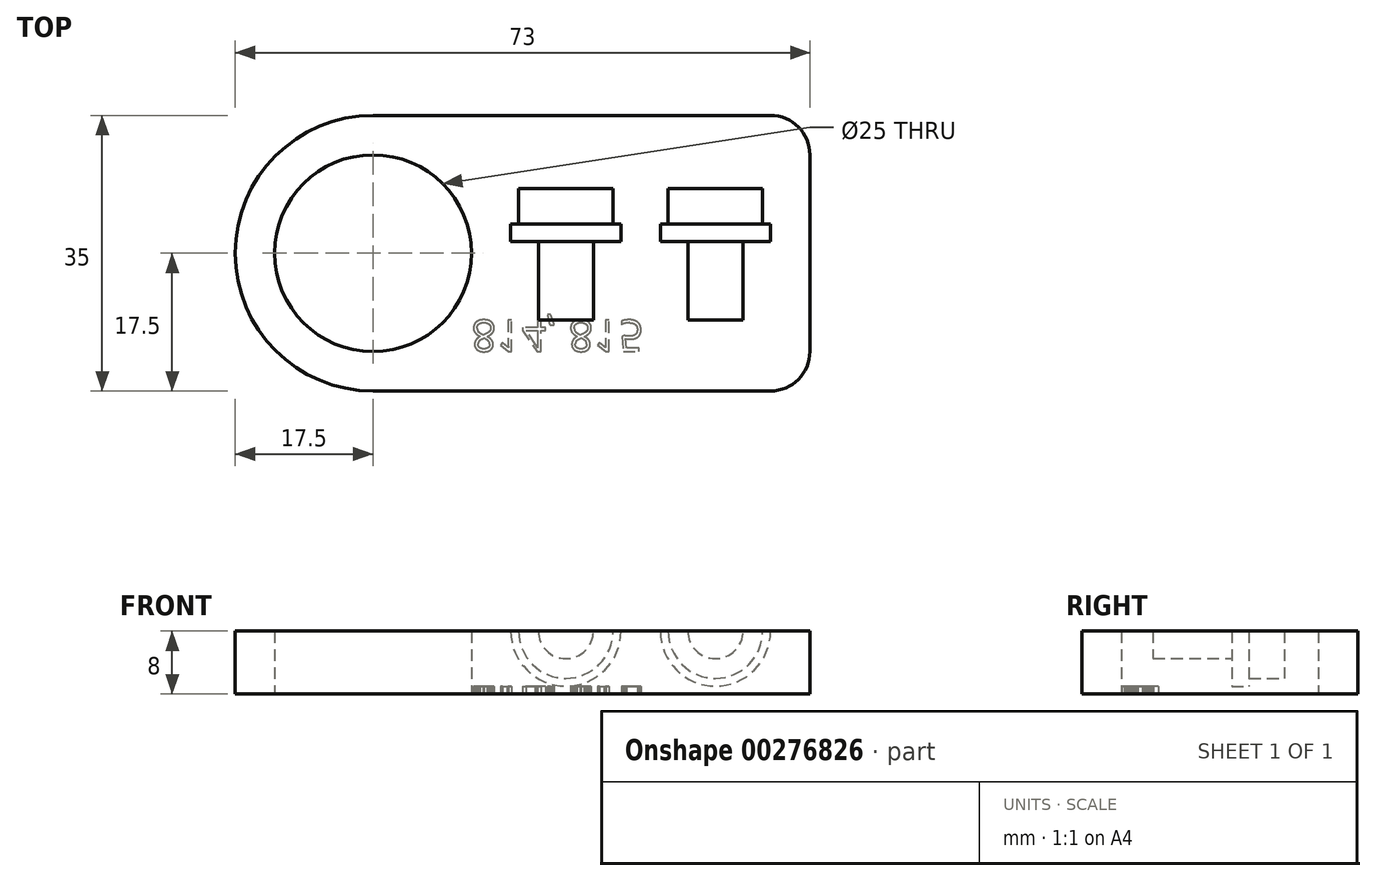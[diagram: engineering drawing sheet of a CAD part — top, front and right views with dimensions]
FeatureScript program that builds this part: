
annotation { "Feature Type Name" : "Feature", "Feature Type Description" : "" }
export const myFeature = defineFeature(function(context is Context, id is Id, definition is map)
    precondition{}
    {
        {
            var Q0;
            Q0=qCreatedBy(makeId("Top.planeOp"),FACE);
            var sketch = newSketch(context, id + "F0", { "sketchPlane" : qUnion([Q0])});
            skLineSegment(sketch, "E0.bottom", {"start": v(17.5, 0) * mm, "end": v(68, 0) * mm});
            skLineSegment(sketch, "E0.top", {"start": v(17.5, 35) * mm, "end": v(68, 35) * mm});
            skLineSegment(sketch, "E0.left", {"start": v(0, 17.5) * mm, "end": v(0, 17.5) * mm});
            skLineSegment(sketch, "E0.right", {"start": v(73, 5) * mm, "end": v(73, 30) * mm});
            skLineSegment(sketch, "E1.bottom", {"start": v(0, 0) * mm, "end": v(17.5, 0) * mm, "construction": true});
            skLineSegment(sketch, "E1.top", {"start": v(0, 17.5) * mm, "end": v(17.5, 17.5) * mm, "construction": true});
            skLineSegment(sketch, "E1.left", {"start": v(0, 0) * mm, "end": v(0, 17.5) * mm, "construction": true});
            skLineSegment(sketch, "E1.right", {"start": v(17.5, 0) * mm, "end": v(17.5, 17.5) * mm, "construction": true});
            skCircle(sketch, "E2", {"center": v(17.5, 17.5) * mm, "radius": 12.5 * mm});
            skPoint(sketch, "E3.visualSharp", {"position": v(0, 0) * mm});
            skArc(sketch, "E3.filletArc", {"start": v(0, 17.5) * mm, "mid": v(5.13, 5.13) * mm, "end": v(17.5, 0) * mm});
            skPoint(sketch, "E4.visualSharp", {"position": v(0, 35) * mm});
            skArc(sketch, "E4.filletArc", {"start": v(17.5, 35) * mm, "mid": v(5.13, 29.87) * mm, "end": v(0, 17.5) * mm});
            skPoint(sketch, "E5.visualSharp", {"position": v(73, 35) * mm});
            skArc(sketch, "E5.filletArc", {"start": v(73, 30) * mm, "mid": v(71.54, 33.54) * mm, "end": v(68, 35) * mm});
            skPoint(sketch, "E6.visualSharp", {"position": v(73, 0) * mm});
            skArc(sketch, "E6.filletArc", {"start": v(68, 0) * mm, "mid": v(71.54, 1.46) * mm, "end": v(73, 5) * mm});
            skSolve(sketch);
        }
        {
            var Q0;
            Q0=makeQuery(id+"F0.imprint","IMPRINT",FACE,{"disambiguationData":[TD([[makeQuery(id+"F0.imprint","IMPRINT",EDGE,{"derivedFrom":sQuery(id+"F0.wireOp",EDGE,"E0.bottom")}),1.0]])]});
            extrude(context, id + "F1", {"entities" : qUnion([Q0]), "depth" : 8 * mm});
        }
        {
            var Q0;
            Q0=makeQuery(id+"F1.opExtrude","CAP_FACE",FACE,{"disambiguationData":[OSD([sQuery(id+"F0.wireOp",EDGE,"E0.bottom"),sQuery(id+"F0.wireOp",EDGE,"E0.top"),sQuery(id+"F0.wireOp",EDGE,"E0.right"),sQuery(id+"F0.wireOp",EDGE,"E2"),sQuery(id+"F0.wireOp",EDGE,"E3.filletArc"),sQuery(id+"F0.wireOp",EDGE,"E4.filletArc"),sQuery(id+"F0.wireOp",EDGE,"E5.filletArc"),sQuery(id+"F0.wireOp",EDGE,"E6.filletArc")])],"isStart":false});
            var sketch = newSketch(context, id + "F2", { "sketchPlane" : qUnion([Q0])});
            skLineSegment(sketch, "E7.bottom", {"start": v(0, 0) * mm, "end": v(42, 0) * mm, "construction": true});
            skLineSegment(sketch, "E7.top", {"start": v(0, 9) * mm, "end": v(42, 9) * mm, "construction": true});
            skLineSegment(sketch, "E7.left", {"start": v(0, 0) * mm, "end": v(0, 9) * mm, "construction": true});
            skLineSegment(sketch, "E7.right", {"start": v(42, 0) * mm, "end": v(42, 9) * mm, "construction": true});
            skLineSegment(sketch, "E8.bottom", {"start": v(42, 9) * mm, "end": v(45.5, 9) * mm});
            skLineSegment(sketch, "E8.left", {"start": v(42, 9) * mm, "end": v(42, 19) * mm});
            skLineSegment(sketch, "E8.right", {"start": v(45.5, 9) * mm, "end": v(45.5, 19) * mm});
            skLineSegment(sketch, "E9.bottom", {"start": v(45.5, 19) * mm, "end": v(49, 19) * mm});
            skLineSegment(sketch, "E9.top", {"start": v(48, 21.2) * mm, "end": v(49, 21.2) * mm});
            skLineSegment(sketch, "E9.left", {"start": v(42, 19) * mm, "end": v(42, 21.2) * mm});
            skLineSegment(sketch, "E9.right", {"start": v(49, 19) * mm, "end": v(49, 21.2) * mm});
            skLineSegment(sketch, "E10.top", {"start": v(42, 25.7) * mm, "end": v(48, 25.7) * mm});
            skLineSegment(sketch, "E10.left", {"start": v(42, 21.2) * mm, "end": v(42, 25.7) * mm});
            skLineSegment(sketch, "E10.right", {"start": v(48, 21.2) * mm, "end": v(48, 25.7) * mm});
            skLineSegment(sketch, "E11", {"start": v(42, 9) * mm, "end": v(61, 9) * mm, "construction": true});
            skLineSegment(sketch, "E12.bottom", {"start": v(61, 9) * mm, "end": v(64.5, 9) * mm});
            skLineSegment(sketch, "E12.left", {"start": v(61, 9) * mm, "end": v(61, 19) * mm});
            skLineSegment(sketch, "E12.right", {"start": v(64.5, 9) * mm, "end": v(64.5, 19) * mm});
            skLineSegment(sketch, "E13.bottom", {"start": v(64.5, 19) * mm, "end": v(68, 19) * mm});
            skLineSegment(sketch, "E13.top", {"start": v(67, 21.2) * mm, "end": v(68, 21.2) * mm});
            skLineSegment(sketch, "E13.left", {"start": v(61, 19) * mm, "end": v(61, 21.2) * mm});
            skLineSegment(sketch, "E13.right", {"start": v(68, 19) * mm, "end": v(68, 21.2) * mm});
            skLineSegment(sketch, "E14.top", {"start": v(61, 25.7) * mm, "end": v(67, 25.7) * mm});
            skLineSegment(sketch, "E14.left", {"start": v(61, 21.2) * mm, "end": v(61, 25.7) * mm});
            skLineSegment(sketch, "E14.right", {"start": v(67, 21.2) * mm, "end": v(67, 25.7) * mm});
            skSolve(sketch);
        }
        {
            var Q0;
            Q0=makeQuery(id+"F2.imprint","IMPRINT",FACE,{"disambiguationData":[TD([[makeQuery(id+"F2.imprint","IMPRINT",EDGE,{"derivedFrom":sQuery(id+"F2.wireOp",EDGE,"E8.bottom")}),1.0]])]});
            var Q1;
            Q1=sQuery(id+"F2.wireOp",EDGE,"E8.left");
            revolve(context, id + "F3", {"operationType" : NewBodyOperationType.REMOVE, "entities" : qUnion([Q0]), "axis" : qUnion([Q1]), "revolveType" : RevolveType.FULL, "oppositeDirection" : true});
        }
        {
            var Q0;
            Q0=makeQuery(id+"F2.imprint","IMPRINT",FACE,{"disambiguationData":[TD([[makeQuery(id+"F2.imprint","IMPRINT",EDGE,{"derivedFrom":sQuery(id+"F2.wireOp",EDGE,"E12.bottom")}),1.0]])]});
            var Q1;
            Q1=sQuery(id+"F2.wireOp",EDGE,"E12.left");
            revolve(context, id + "F4", {"operationType" : NewBodyOperationType.REMOVE, "entities" : qUnion([Q0]), "axis" : qUnion([Q1]), "revolveType" : RevolveType.FULL, "oppositeDirection" : true});
        }
        {
            var Q0;
            Q0=makeQuery(id+"F1.opExtrude","CAP_FACE",FACE,{"disambiguationData":[OSD([sQuery(id+"F0.wireOp",EDGE,"E0.bottom"),sQuery(id+"F0.wireOp",EDGE,"E0.top"),sQuery(id+"F0.wireOp",EDGE,"E0.right"),sQuery(id+"F0.wireOp",EDGE,"E2"),sQuery(id+"F0.wireOp",EDGE,"E3.filletArc"),sQuery(id+"F0.wireOp",EDGE,"E4.filletArc"),sQuery(id+"F0.wireOp",EDGE,"E5.filletArc"),sQuery(id+"F0.wireOp",EDGE,"E6.filletArc")])],"isStart":true});
            var sketch = newSketch(context, id + "F5", { "sketchPlane" : qUnion([Q0])});
            skLineSegment(sketch, "E15.bottom", {"start": v(0, 0) * mm, "end": v(30, 0) * mm, "construction": true});
            skLineSegment(sketch, "E15.top", {"start": v(0, -5) * mm, "end": v(30, -5) * mm, "construction": true});
            skLineSegment(sketch, "E15.left", {"start": v(0, 0) * mm, "end": v(0, -5) * mm, "construction": true});
            skLineSegment(sketch, "E15.right", {"start": v(30, 0) * mm, "end": v(30, -5) * mm, "construction": true});
            skText(sketch, "E16", { "text": "814, 815", "fontName": "OpenSans-Regular.ttf"});
            skPoint(sketch, "E16.secondSnap0", {"position": v(51.9, 6.67) * mm});
            const initialGuessF5  = {"E16": [0.03, -0.009, 1, 0, 0.004]};
            skSetInitialGuess(sketch, initialGuessF5);
            skSolve(sketch);
        }
        {
            var Q0;
            Q0 = qSketchRegion(id + "F5", true);
            extrude(context, id + "F6", {"entities" : qUnion([Q0]), "operationType" : NewBodyOperationType.REMOVE, "oppositeDirection" : true, "depth" : 1 * mm});
        }
    });
